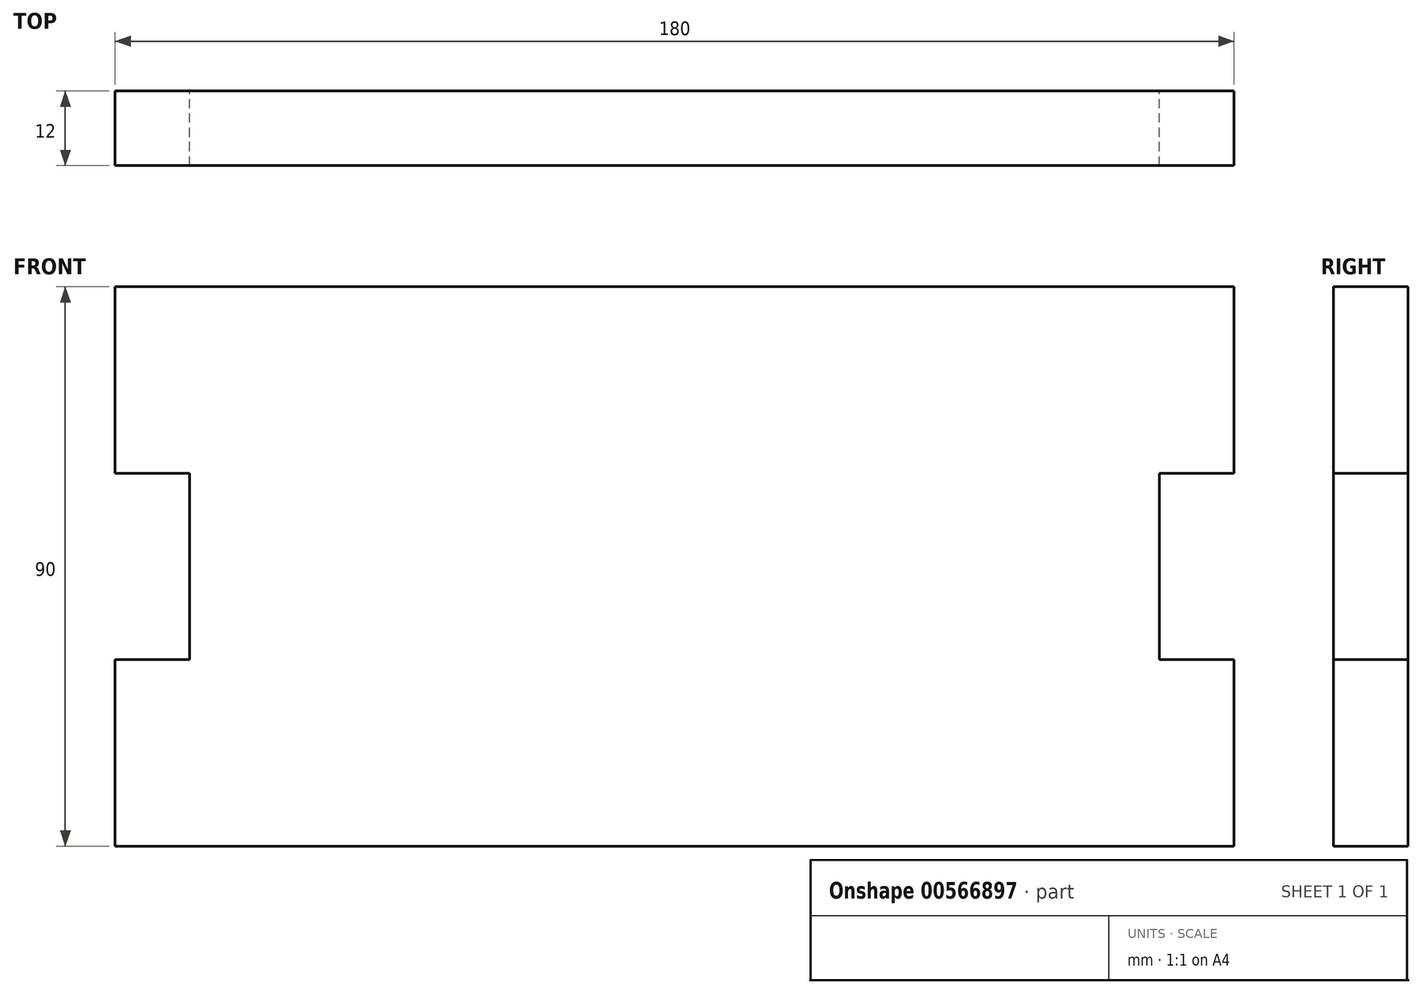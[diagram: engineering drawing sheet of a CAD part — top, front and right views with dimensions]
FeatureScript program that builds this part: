
annotation { "Feature Type Name" : "Feature", "Feature Type Description" : "" }
export const myFeature = defineFeature(function(context is Context, id is Id, definition is map)
    precondition{}
    {
        {
            var Q0;
            Q0=qCreatedBy(makeId("Front.planeOp"),FACE);
            var sketch = newSketch(context, id + "F0", { "sketchPlane" : qUnion([Q0])});
            skLineSegment(sketch, "E0", {"start": v(0, 0) * mm, "end": v(0, 30) * mm});
            skLineSegment(sketch, "E1", {"start": v(0, 30) * mm, "end": v(12, 30) * mm});
            skLineSegment(sketch, "E2", {"start": v(12, 30) * mm, "end": v(12, 60) * mm});
            skLineSegment(sketch, "E3", {"start": v(12, 60) * mm, "end": v(0, 60) * mm});
            skLineSegment(sketch, "E4", {"start": v(0, 60) * mm, "end": v(0, 90) * mm});
            skLineSegment(sketch, "E5", {"start": v(0, 90) * mm, "end": v(180, 90) * mm});
            skLineSegment(sketch, "E6", {"start": v(0, 0) * mm, "end": v(180, 0) * mm});
            skLineSegment(sketch, "E7", {"start": v(180, 90) * mm, "end": v(180, 60) * mm});
            skLineSegment(sketch, "E8", {"start": v(180, 60) * mm, "end": v(168, 60) * mm});
            skLineSegment(sketch, "E9", {"start": v(168, 60) * mm, "end": v(168, 30) * mm});
            skLineSegment(sketch, "E10", {"start": v(168, 30) * mm, "end": v(180, 30) * mm});
            skLineSegment(sketch, "E11", {"start": v(180, 30) * mm, "end": v(180, 0) * mm});
            skSolve(sketch);
        }
        {
            var Q0;
            Q0=makeQuery(id+"F0.imprint","IMPRINT",FACE,{"disambiguationData":[TD([[makeQuery(id+"F0.imprint","IMPRINT",EDGE,{"derivedFrom":sQuery(id+"F0.wireOp",EDGE,"E0")}),-1.0]])]});
            extrude(context, id + "F1", {"entities" : qUnion([Q0]), "depth" : 12 * mm, "offsetDistance" : 25 * mm});
        }
    });
